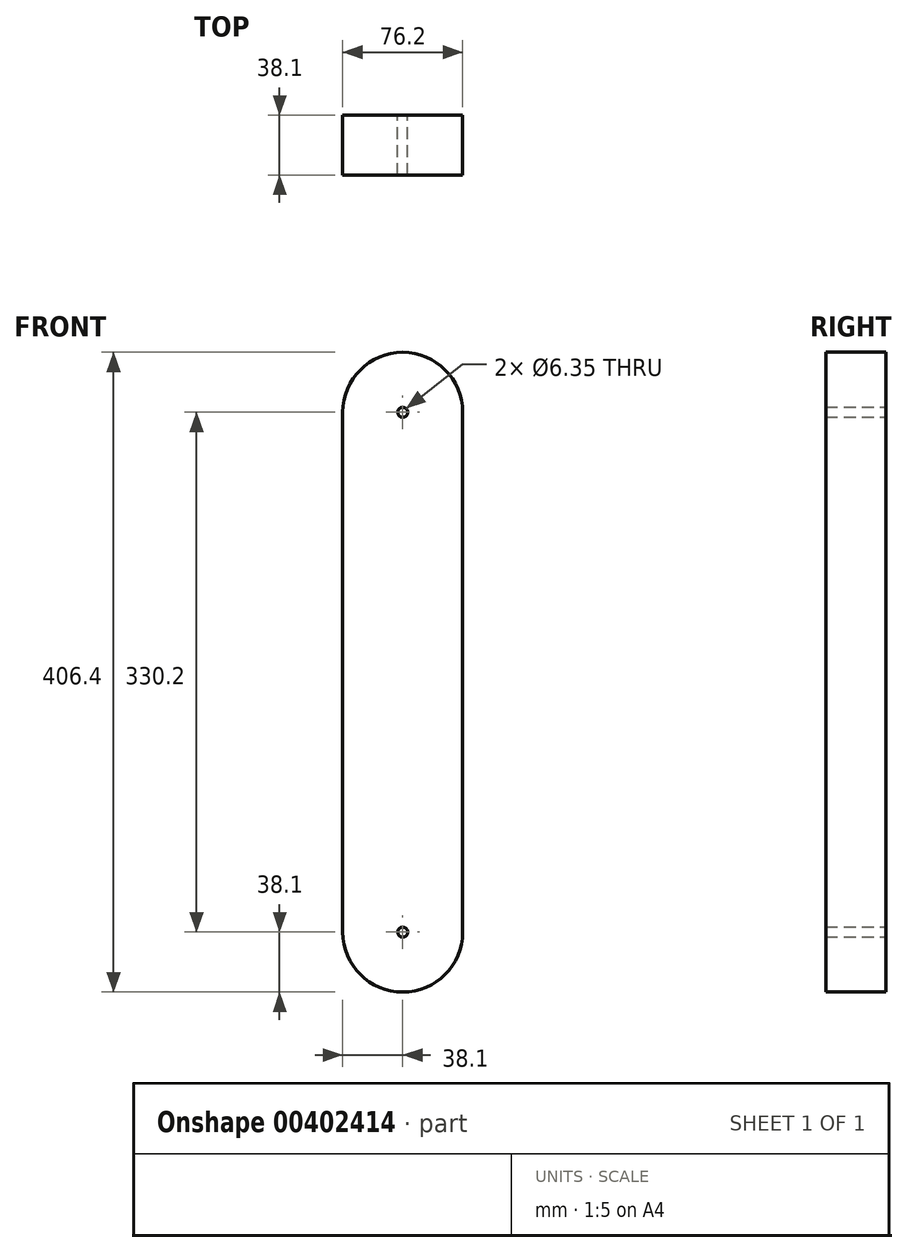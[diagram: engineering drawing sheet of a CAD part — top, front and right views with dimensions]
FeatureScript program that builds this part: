
annotation { "Feature Type Name" : "Feature", "Feature Type Description" : "" }
export const myFeature = defineFeature(function(context is Context, id is Id, definition is map)
    precondition{}
    {
        {
            var Q0;
            Q0=qCreatedBy(makeId("Front.planeOp"),FACE);
            var sketch = newSketch(context, id + "F0", { "sketchPlane" : qUnion([Q0])});
            skCircle(sketch, "E0", {"center": v(0, 0) * mm, "radius": 38.1 * mm});
            skCircle(sketch, "E1", {"center": v(0, 330.2) * mm, "radius": 38.1 * mm});
            skLineSegment(sketch, "E2", {"start": v(38.1, 330.2) * mm, "end": v(38.1, 0) * mm});
            skLineSegment(sketch, "E3", {"start": v(-38.1, 330.2) * mm, "end": v(-38.1, 0) * mm});
            skCircle(sketch, "E4", {"center": v(0, 0) * mm, "radius": 3.18 * mm});
            skCircle(sketch, "E5", {"center": v(0, 330.2) * mm, "radius": 3.18 * mm});
            skSolve(sketch);
        }
        {
            var Q0;
            {var subQ0=sQuery(id+"F0.wireOp",EDGE,"E0");var subQ1=makeQuery(id+"F0.imprint","INTERSECT",VERTEX,{"derivedFrom":[subQ0,sQuery(id+"F0.wireOp",EDGE,"E2")]});Q0=makeQuery(id+"F0.imprint","IMPRINT",FACE,{"disambiguationData":[TD([[makeQuery(id+"F0.imprint","IMPRINT",EDGE,{"disambiguationData":[TD([[subQ1,-1.0]])],"derivedFrom":subQ0}),1.0]])]});}
            var Q1;
            {var subQ0=sQuery(id+"F0.wireOp",EDGE,"E2");Q1=makeQuery(id+"F0.imprint","IMPRINT",FACE,{"disambiguationData":[TD([[makeQuery(id+"F0.imprint","IMPRINT",EDGE,{"derivedFrom":subQ0}),-1.0]])]});}
            var Q2;
            {var subQ0=sQuery(id+"F0.wireOp",EDGE,"E1");var subQ1=makeQuery(id+"F0.imprint","INTERSECT",VERTEX,{"derivedFrom":[subQ0,sQuery(id+"F0.wireOp",EDGE,"E2")]});Q2=makeQuery(id+"F0.imprint","IMPRINT",FACE,{"disambiguationData":[TD([[makeQuery(id+"F0.imprint","IMPRINT",EDGE,{"disambiguationData":[TD([[subQ1,1.0]])],"derivedFrom":subQ0}),1.0]])]});}
            extrude(context, id + "F1", {"entities" : qUnion([Q0, Q1, Q2]), "depth" : 38.1 * mm});
        }
    });
